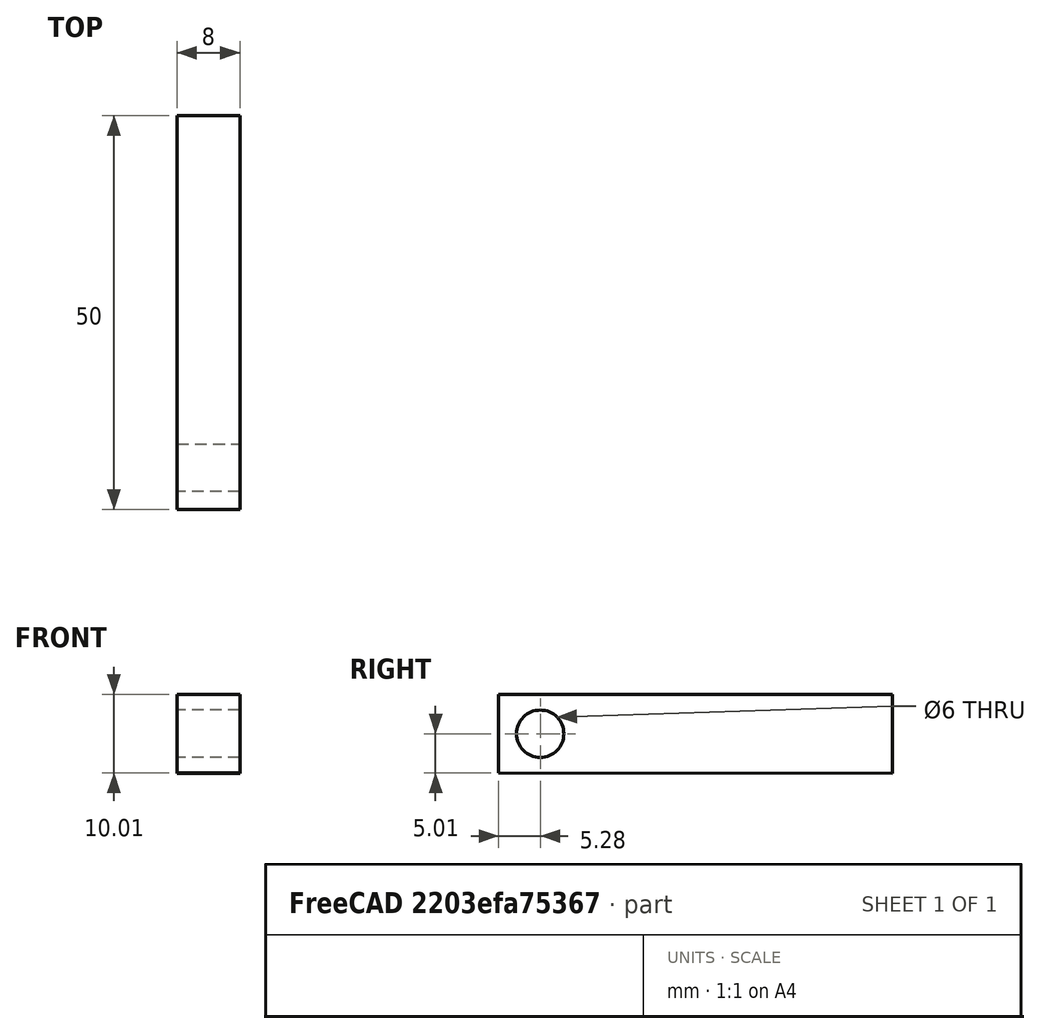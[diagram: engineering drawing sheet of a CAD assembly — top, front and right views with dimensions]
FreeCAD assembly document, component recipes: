
FREECAD ASSEMBLY — COMPONENT RECIPES ("Assembly_000")

This assembly document has 2 components, labeled P0..P1 below (a component is one placed body or linked part). 1 of them carries a construction recipe — the FreeCAD feature program that regenerates the part from scratch, quoted from this document or its linked companion documents; the rest are supplied as boundary geometry only. No exploded tour is included for this assembly.
COMPONENT P0 — geometry summary ("Assembly"; no construction recipe available for this part):
  bounding box: 79.9 x 42.4 x 8.0 mm
  tessellated surface: 64 triangles
  volume: 7846377169233351079574818507433831878592849867333782994230693877161723273322418716113109793577529780319843425288349404680734961459834699099801172748321947648 mm^3 (28937532180173124320471295018135323914281411310191428105594351002898969947493413668021855981265883509369878004698196808793027582374808536219985353574973440% of its bounding box)
  symmetry: mirror-symmetric across its x mid-plane
COMPONENT P1 — recipe-attached ("Body", modeled in this document).
Construction recipe (the document's own serialized feature program — sketch geometry with constraints, then the solid features built on it; lengths are millimeters unless a unit is written):

FEATURE [PartDesign::CoordinateSystem] LCS_0
  AttacherType = Attacher::AttachEngine3D
  MapMode = 2
  Support = -> [X_Axis001]
FEATURE [Sketcher::SketchObject] Sketch
  FullyConstrained = false
  MapMode = 5
  Placement = pos=(0,0,0) rot=(0.57735,0.57735,0.57735;2.0944rad)
  Support = -> [YZ_Plane001]
  sketch-geometry (5):
    g0: LineSegment StartX=-5.27726 StartY=5.00146 StartZ=0 EndX=44.7227 EndY=4.98767 EndZ=0
    g1: LineSegment StartX=44.7227 StartY=4.98767 StartZ=0 EndX=44.72 EndY=-5.01233 EndZ=0
    g2: LineSegment StartX=44.72 StartY=-5.01233 StartZ=0 EndX=-5.28002 EndY=-4.99854 EndZ=0
    g3: LineSegment StartX=-5.28002 StartY=-4.99854 StartZ=0 EndX=-5.27726 EndY=5.00146 EndZ=0
    g4: Circle CenterX=0 CenterY=0 CenterZ=0 NormalX=0 NormalY=0 NormalZ=1 AngleXU=0 Radius=3
  constraints (13):
    c: Coincident(g0,g1)
    c: Coincident(g1,g2)
    c: Coincident(g2,g3)
    c: Coincident(g3,g0)
    c: Distance(g0,g2) = 10
    c: Distance(g0,g0) = 50
    c: Parallel(g0,g2)
    c: Parallel(g3,g1)
    c: Perpendicular(g0,g1)
    c: Coincident(g4,g-1)
    c: Radius(g4) = 3
    c: Distance(g4,g0) = 45
    c: Distance(g4,g1) = 45
FEATURE [PartDesign::Pad] Pad
  Direction = (1,-2e-16,3e-16)
  Length = 8
  Length2 = 10
  Placement = pos=(0,0,0) rot=(1,1,1;2.0944rad)
  Profile = -> Sketch
  ReferenceAxis = -> Sketch [N_Axis]
  Type = 0
FEATURE [PartDesign::Body] Body
  Group = -> [LCS_0,Sketch,Pad]
  Origin = -> Origin001
  Placement = pos=(-52,0,0) rot=(0,0,1;0rad)
  Tip = -> Pad
PROVENANCE & LICENSES
A FreeCAD (.FCStd) document from a public repository crawl; recipes are the document's own serialized feature recipes (and, for linked parts, companion documents' recipes).
License: as declared in the source repository (recorded in the dataset sidecar).
